# Revit family: IEK_Основание бетонное для мачты
name_source: partatom
category: Обобщенные модели
units: mm (PartAtom-declared; Revit-internal decimal feet)

## family parameters
Может служить основой для арматурных стержней = Нет
Общий = Да
Основа = Грань
При загрузке вырезать с полостями = Нет
Размер круглого соединителя = Использовать диаметр
Тип детали = Нормальный
Точка расчета площади = Нет

## types (1)
- _
    ADSK_URL страницы изделия = https://www.iek.ru
    ADSK_Версия Revit = 2019
    ADSK_Версия семейства = 1.0
    ADSK_Группирование = VIII. ЭЛЕМЕНТЫ ВНЕШНЕЙ МОЛНИЕЗАЩИТЫ
    ADSK_Единица измерения = шт
    ADSK_Завод-изготовитель = IEK
    ADSK_Код изделия = ZML10D-CB-01
    ADSK_Масса = 38
    ADSK_Материал = RAL 9005 Чёрный янтарь
    ADSK_Материал наименование = Бетон
    ADSK_Наименование = Основание бетонное для мачты IEK
    IEK_URL = https://www.iek.ru
    IEK_Описание = Основание бетонное для мачты малое товарного знака IEK используется для установки на плоской кровле молниеприемной мачты высотой до 4 метров. Применяется для выполнения молниезащиты отдельных выступающих на кровле объектов: вентиляционных шахт, элементов систем кондиционирования и т.д.
    IEK_Цена за единицу = 6700
    Отметка по умолчанию = 0 мм
